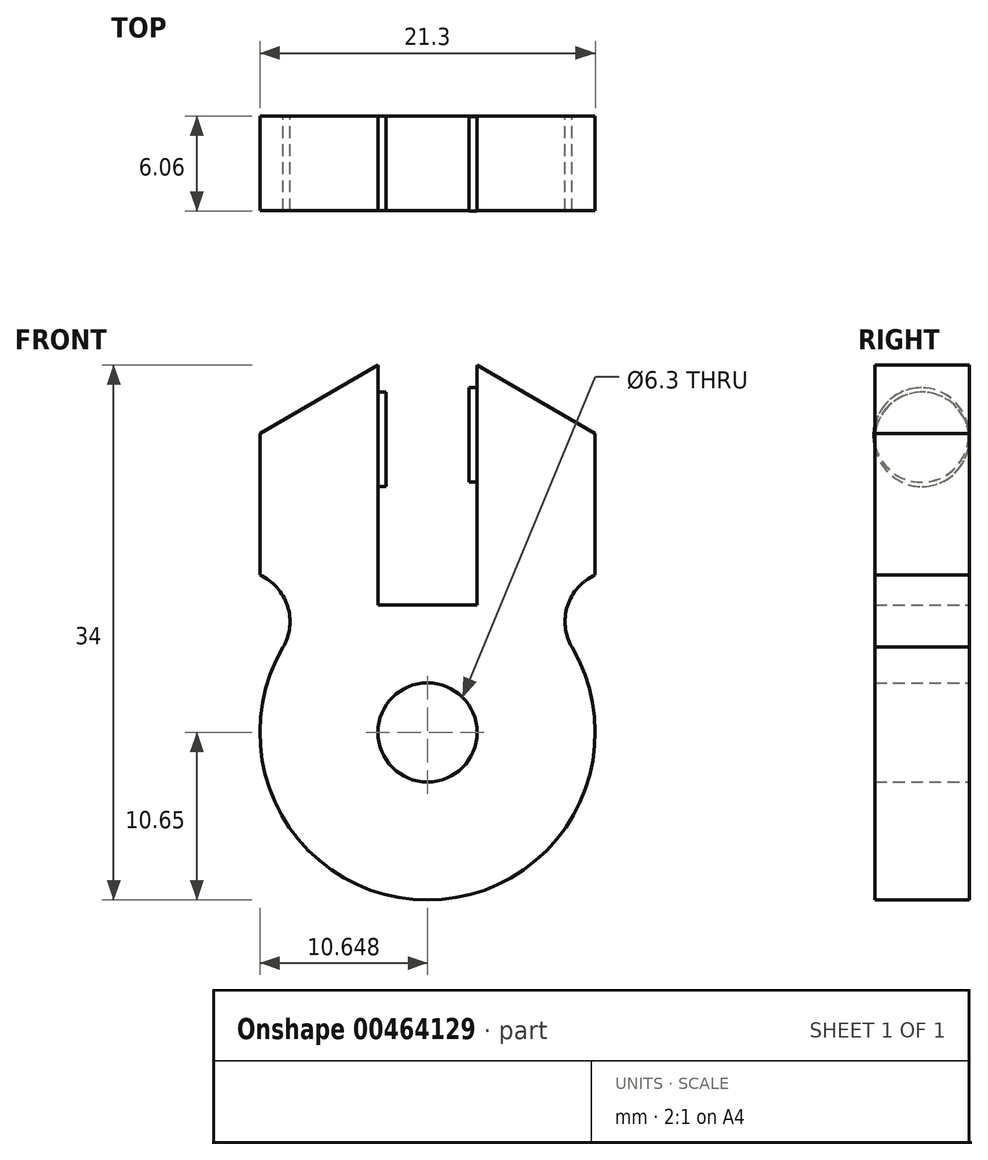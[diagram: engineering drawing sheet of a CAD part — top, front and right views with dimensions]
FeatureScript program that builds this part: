
annotation { "Feature Type Name" : "Feature", "Feature Type Description" : "" }
export const myFeature = defineFeature(function(context is Context, id is Id, definition is map)
    precondition{}
    {
        {
            var Q0;
            Q0=qCreatedBy(makeId("Front.planeOp"),FACE);
            var sketch = newSketch(context, id + "F0", { "sketchPlane" : qUnion([Q0])});
            skArc(sketch, "E0", {"start": v(-38.91, 42.77) * mm, "mid": v(-35.76, 21.95) * mm, "end": v(-32.61, 42.77) * mm});
            skCircle(sketch, "E1", {"center": v(-35.76, 32.6) * mm, "radius": 3.15 * mm});
            skLineSegment(sketch, "E2", {"start": v(-35.76, 32.6) * mm, "end": v(-35.76, 35.75) * mm});
            skLineSegment(sketch, "E3", {"start": v(-35.76, 40.7) * mm, "end": v(-32.61, 40.7) * mm});
            skLineSegment(sketch, "E4", {"start": v(-35.76, 40.7) * mm, "end": v(-38.91, 40.7) * mm});
            skLineSegment(sketch, "E5", {"start": v(-38.91, 40.7) * mm, "end": v(-38.91, 55.95) * mm});
            skLineSegment(sketch, "E6", {"start": v(-32.61, 40.7) * mm, "end": v(-32.61, 55.95) * mm});
            skLineSegment(sketch, "E7", {"start": v(-46.41, 51.6) * mm, "end": v(-38.91, 55.95) * mm});
            skLineSegment(sketch, "E8", {"start": v(-46.41, 51.6) * mm, "end": v(-46.41, 42.6) * mm});
            skLineSegment(sketch, "E9", {"start": v(-35.76, 32.6) * mm, "end": v(-38.91, 32.6) * mm});
            skArc(sketch, "E10", {"start": v(-44.93, 38.02) * mm, "mid": v(-44.65, 40.64) * mm, "end": v(-46.41, 42.6) * mm});
            skArc(sketch, "E11.MirrorCS", {"start": v(-26.6, 38.02) * mm, "mid": v(-26.87, 40.64) * mm, "end": v(-25.11, 42.6) * mm});
            skLineSegment(sketch, "E12.MirrorCS", {"start": v(-25.11, 51.6) * mm, "end": v(-25.11, 42.6) * mm});
            skLineSegment(sketch, "E13.MirrorCS", {"start": v(-25.11, 51.6) * mm, "end": v(-32.61, 55.95) * mm});
            skSolve(sketch);
        }
        {
            var Q0;
            Q0 = qSketchRegion(id + "F0", true);
            extrude(context, id + "F1", {"entities" : qUnion([Q0]), "depth" : 6 * mm});
        }
        {
            var Q0;
            Q0=makeQuery(id+"F1.opExtrude","SWEPT_FACE",FACE,{"disambiguationData":[OSD([sQuery(id+"F0.wireOp",EDGE,"E6")])]});
            var sketch = newSketch(context, id + "F2", { "sketchPlane" : qUnion([Q0])});
            skLineSegment(sketch, "E14", {"start": v(3, 54.49) * mm, "end": v(3, 54.45) * mm});
            skPoint(sketch, "E14.endSnap0", {"position": v(3, 55.95) * mm});
            skCircle(sketch, "E15", {"center": v(3.06, 51.5) * mm, "radius": 3 * mm});
            skSolve(sketch);
        }
        {
            var Q0;
            Q0 = qSketchRegion(id + "F2", true);
            extrude(context, id + "F3", {"entities" : qUnion([Q0]), "operationType" : NewBodyOperationType.ADD, "depth" : .5 * mm});
        }
        {
            var Q0;
            Q0=makeQuery(id+"F1.opExtrude","SWEPT_FACE",FACE,{"disambiguationData":[OSD([sQuery(id+"F0.wireOp",EDGE,"E5")])]});
            var sketch = newSketch(context, id + "F4", { "sketchPlane" : qUnion([Q0])});
            skLineSegment(sketch, "E16", {"start": v(-3, 55.95) * mm, "end": v(-3, 54.45) * mm});
            skCircle(sketch, "E17", {"center": v(-3.02, 51.21) * mm, "radius": 3 * mm});
            skSolve(sketch);
        }
        {
            var Q0;
            Q0 = qSketchRegion(id + "F4", true);
            extrude(context, id + "F5", {"entities" : qUnion([Q0]), "operationType" : NewBodyOperationType.ADD, "depth" : .5 * mm});
        }
        {
            var Q0;
            Q0 = qSketchRegion(id + "F0", true);
            extrude(context, id + "F6", {"entities" : qUnion([Q0]), "operationType" : NewBodyOperationType.ADD, "depth" : 6 * mm});
        }
    });
